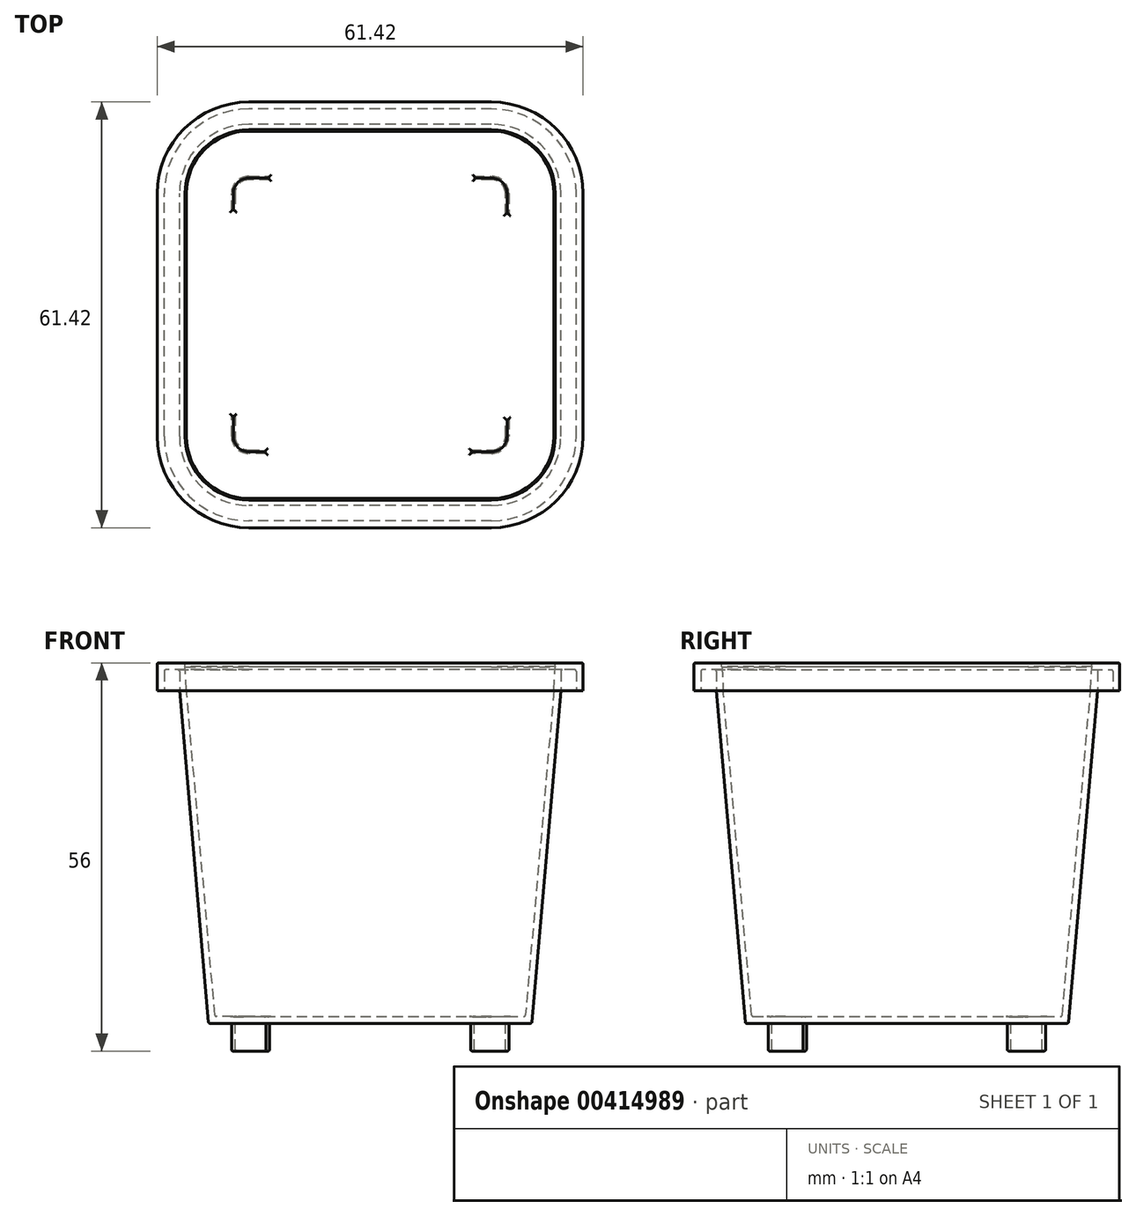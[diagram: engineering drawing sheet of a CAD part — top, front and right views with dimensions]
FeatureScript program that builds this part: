
annotation { "Feature Type Name" : "Feature", "Feature Type Description" : "" }
export const myFeature = defineFeature(function(context is Context, id is Id, definition is map)
    precondition{}
    {
        {
            var Q0;
            Q0=qCreatedBy(makeId("Top.planeOp"),FACE);
            var sketch = newSketch(context, id + "F0", { "sketchPlane" : qUnion([Q0])});
            skLineSegment(sketch, "E0.bottom", {"start": v(17.5, -27.5) * mm, "end": v(-17.5, -27.5) * mm});
            skLineSegment(sketch, "E0.top", {"start": v(17.5, 27.5) * mm, "end": v(-17.5, 27.5) * mm});
            skLineSegment(sketch, "E0.left", {"start": v(27.5, -17.5) * mm, "end": v(27.5, 17.5) * mm});
            skLineSegment(sketch, "E0.right", {"start": v(-27.5, -17.5) * mm, "end": v(-27.5, 17.5) * mm});
            skPoint(sketch, "E0.middle", {"position": v(0, 0) * mm});
            skPoint(sketch, "E1.visualSharp", {"position": v(-27.5, 27.5) * mm});
            skArc(sketch, "E1.filletArc", {"start": v(-17.5, 27.5) * mm, "mid": v(-24.57, 24.57) * mm, "end": v(-27.5, 17.5) * mm});
            skPoint(sketch, "E2.visualSharp", {"position": v(-27.5, -27.5) * mm});
            skArc(sketch, "E2.filletArc", {"start": v(-27.5, -17.5) * mm, "mid": v(-24.57, -24.57) * mm, "end": v(-17.5, -27.5) * mm});
            skPoint(sketch, "E3.visualSharp", {"position": v(27.5, -27.5) * mm});
            skArc(sketch, "E3.filletArc", {"start": v(17.5, -27.5) * mm, "mid": v(24.57, -24.57) * mm, "end": v(27.5, -17.5) * mm});
            skPoint(sketch, "E4.visualSharp", {"position": v(27.5, 27.5) * mm});
            skArc(sketch, "E4.filletArc", {"start": v(27.5, 17.5) * mm, "mid": v(24.57, 24.57) * mm, "end": v(17.5, 27.5) * mm});
            skSolve(sketch);
        }
        {
            var Q0;
            Q0 = qSketchRegion(id + "F0", true);
            extrude(context, id + "F1", {"entities" : qUnion([Q0]), "depth" : 4 * mm, "hasDraft" : true, "draftAngle" : 3 * degree, "hasSecondDirectionDraft" : true, "secondDirectionDraftAngle" : 3 * degree});
        }
        {
            var Q0;
            Q0=makeQuery(id+"F1.opExtrude","CAP_FACE",FACE,{"disambiguationData":[OSD([sQuery(id+"F0.wireOp",EDGE,"E0.bottom"),sQuery(id+"F0.wireOp",EDGE,"E0.top"),sQuery(id+"F0.wireOp",EDGE,"E0.left"),sQuery(id+"F0.wireOp",EDGE,"E0.right"),sQuery(id+"F0.wireOp",EDGE,"E1.filletArc"),sQuery(id+"F0.wireOp",EDGE,"E2.filletArc"),sQuery(id+"F0.wireOp",EDGE,"E3.filletArc"),sQuery(id+"F0.wireOp",EDGE,"E4.filletArc")])],"isStart":true});
            extrude(context, id + "F2", {"entities" : qUnion([Q0]), "operationType" : NewBodyOperationType.ADD, "depth" : 48 * mm, "hasDraft" : true, "draftAngle" : 5 * degree, "draftPullDirection" : true});
        }
        {
            var Q0;
            Q0=makeQuery(id+"F1.opExtrude","CAP_FACE",FACE,{"disambiguationData":[OSD([sQuery(id+"F0.wireOp",EDGE,"E0.bottom"),sQuery(id+"F0.wireOp",EDGE,"E0.top"),sQuery(id+"F0.wireOp",EDGE,"E0.left"),sQuery(id+"F0.wireOp",EDGE,"E0.right"),sQuery(id+"F0.wireOp",EDGE,"E1.filletArc"),sQuery(id+"F0.wireOp",EDGE,"E2.filletArc"),sQuery(id+"F0.wireOp",EDGE,"E3.filletArc"),sQuery(id+"F0.wireOp",EDGE,"E4.filletArc")])],"isStart":false});
            shell(context, id + "F3", {"entities" : qUnion([Q0]), "thickness" : 1 * mm});
        }
        {
            var Q0;
            Q0=makeQuery(id+"F1.opExtrude","CAP_FACE",FACE,{"disambiguationData":[OSD([sQuery(id+"F0.wireOp",EDGE,"E0.bottom"),sQuery(id+"F0.wireOp",EDGE,"E0.top"),sQuery(id+"F0.wireOp",EDGE,"E0.left"),sQuery(id+"F0.wireOp",EDGE,"E0.right"),sQuery(id+"F0.wireOp",EDGE,"E1.filletArc"),sQuery(id+"F0.wireOp",EDGE,"E2.filletArc"),sQuery(id+"F0.wireOp",EDGE,"E3.filletArc"),sQuery(id+"F0.wireOp",EDGE,"E4.filletArc")])],"isStart":false});
            var sketch = newSketch(context, id + "F4", { "sketchPlane" : qUnion([Q0])});
            skLineSegment(sketch, "E5.0", {"start": v(17.5, 30.7) * mm, "end": v(-17.5, 30.7) * mm});
            skArc(sketch, "E5.1", {"start": v(30.7, 17.5) * mm, "mid": v(26.84, 26.84) * mm, "end": v(17.5, 30.7) * mm});
            skArc(sketch, "E5.2", {"start": v(-17.5, 30.7) * mm, "mid": v(-26.84, 26.84) * mm, "end": v(-30.7, 17.5) * mm});
            skLineSegment(sketch, "E5.3", {"start": v(30.7, -17.5) * mm, "end": v(30.7, 17.5) * mm});
            skLineSegment(sketch, "E5.4", {"start": v(-30.7, -17.5) * mm, "end": v(-30.7, 17.5) * mm});
            skArc(sketch, "E5.5", {"start": v(-30.7, -17.5) * mm, "mid": v(-26.84, -26.84) * mm, "end": v(-17.5, -30.7) * mm});
            skLineSegment(sketch, "E5.6", {"start": v(17.5, -30.7) * mm, "end": v(-17.5, -30.7) * mm});
            skArc(sketch, "E5.7", {"start": v(17.5, -30.7) * mm, "mid": v(26.84, -26.84) * mm, "end": v(30.7, -17.5) * mm});
            skArc(sketch, "E6.0", {"start": v(-17.5, 26.7) * mm, "mid": v(-24.01, 24.01) * mm, "end": v(-26.7, 17.5) * mm});
            skLineSegment(sketch, "E7.0", {"start": v(-26.7, -17.5) * mm, "end": v(-26.7, 17.5) * mm});
            skArc(sketch, "E8.0", {"start": v(-26.7, -17.5) * mm, "mid": v(-24.01, -24.01) * mm, "end": v(-17.5, -26.7) * mm});
            skLineSegment(sketch, "E9.0", {"start": v(17.5, -26.7) * mm, "end": v(-17.5, -26.7) * mm});
            skArc(sketch, "E10.0", {"start": v(17.5, -26.7) * mm, "mid": v(24.01, -24.01) * mm, "end": v(26.7, -17.5) * mm});
            skLineSegment(sketch, "E11.0", {"start": v(26.7, -17.5) * mm, "end": v(26.7, 17.5) * mm});
            skArc(sketch, "E12.0", {"start": v(26.7, 17.5) * mm, "mid": v(24.01, 24.01) * mm, "end": v(17.5, 26.7) * mm});
            skLineSegment(sketch, "E13.0", {"start": v(17.5, 26.7) * mm, "end": v(-17.5, 26.7) * mm});
            skSolve(sketch);
        }
        {
            var Q0;
            Q0 = qSketchRegion(id + "F4", true);
            extrude(context, id + "F5", {"entities" : qUnion([Q0]), "operationType" : NewBodyOperationType.ADD, "oppositeDirection" : true, "depth" : 4 * mm});
        }
        {
            var Q0;
            Q0=makeQuery(id+"F5.opExtrude","CAP_FACE",FACE,{"disambiguationData":[OSD([sQuery(id+"F4.wireOp",EDGE,"E5.0"),sQuery(id+"F4.wireOp",EDGE,"E5.1"),sQuery(id+"F4.wireOp",EDGE,"E5.2"),sQuery(id+"F4.wireOp",EDGE,"E5.3"),sQuery(id+"F4.wireOp",EDGE,"E5.4"),sQuery(id+"F4.wireOp",EDGE,"E5.5"),sQuery(id+"F4.wireOp",EDGE,"E5.6"),sQuery(id+"F4.wireOp",EDGE,"E5.7"),sQuery(id+"F4.wireOp",EDGE,"E6.0"),sQuery(id+"F4.wireOp",EDGE,"E7.0"),sQuery(id+"F4.wireOp",EDGE,"E8.0"),sQuery(id+"F4.wireOp",EDGE,"E9.0"),sQuery(id+"F4.wireOp",EDGE,"E10.0"),sQuery(id+"F4.wireOp",EDGE,"E11.0"),sQuery(id+"F4.wireOp",EDGE,"E12.0"),sQuery(id+"F4.wireOp",EDGE,"E13.0")])],"isStart":false});
            var sketch = newSketch(context, id + "F6", { "sketchPlane" : qUnion([Q0])});
            skArc(sketch, "E14.0", {"start": v(-27.5, 17.5) * mm, "mid": v(-24.57, 24.57) * mm, "end": v(-17.5, 27.5) * mm});
            skLineSegment(sketch, "E14.1", {"start": v(17.5, 27.5) * mm, "end": v(-17.5, 27.5) * mm});
            skArc(sketch, "E14.2", {"start": v(-17.5, -27.5) * mm, "mid": v(-24.57, -24.57) * mm, "end": v(-27.5, -17.5) * mm});
            skLineSegment(sketch, "E14.3", {"start": v(-27.5, 17.5) * mm, "end": v(-27.5, -17.5) * mm});
            skLineSegment(sketch, "E14.4", {"start": v(27.5, 17.5) * mm, "end": v(27.5, -17.5) * mm});
            skArc(sketch, "E14.5", {"start": v(17.5, 27.5) * mm, "mid": v(24.57, 24.57) * mm, "end": v(27.5, 17.5) * mm});
            skArc(sketch, "E14.6", {"start": v(27.5, -17.5) * mm, "mid": v(24.57, -24.57) * mm, "end": v(17.5, -27.5) * mm});
            skLineSegment(sketch, "E14.7", {"start": v(17.5, -27.5) * mm, "end": v(-17.5, -27.5) * mm});
            skArc(sketch, "E15.0", {"start": v(-29.7, 17.5) * mm, "mid": v(-26.13, 26.13) * mm, "end": v(-17.5, 29.7) * mm});
            skLineSegment(sketch, "E15.1", {"start": v(-29.7, 17.5) * mm, "end": v(-29.7, -17.5) * mm});
            skArc(sketch, "E16.0", {"start": v(-17.5, -29.7) * mm, "mid": v(-26.13, -26.13) * mm, "end": v(-29.7, -17.5) * mm});
            skLineSegment(sketch, "E16.1", {"start": v(17.5, -29.7) * mm, "end": v(-17.5, -29.7) * mm});
            skLineSegment(sketch, "E16.2", {"start": v(17.5, 29.7) * mm, "end": v(-17.5, 29.7) * mm});
            skArc(sketch, "E16.3", {"start": v(17.5, 29.7) * mm, "mid": v(26.13, 26.13) * mm, "end": v(29.7, 17.5) * mm});
            skLineSegment(sketch, "E16.4", {"start": v(29.7, 17.5) * mm, "end": v(29.7, -17.5) * mm});
            skArc(sketch, "E16.5", {"start": v(29.7, -17.5) * mm, "mid": v(26.13, -26.13) * mm, "end": v(17.5, -29.7) * mm});
            skSolve(sketch);
        }
        {
            var Q0;
            Q0 = qSketchRegion(id + "F6", true);
            extrude(context, id + "F7", {"entities" : qUnion([Q0]), "operationType" : NewBodyOperationType.REMOVE, "oppositeDirection" : true, "depth" : 3 * mm});
        }
        {
            var Q0;
            Q0=makeQuery(id+"F2.opExtrude","CAP_FACE",FACE,{"disambiguationData":[OSD([sQuery(id+"F0.wireOp",EDGE,"E0.bottom"),sQuery(id+"F0.wireOp",EDGE,"E0.top"),sQuery(id+"F0.wireOp",EDGE,"E0.left"),sQuery(id+"F0.wireOp",EDGE,"E0.right"),sQuery(id+"F0.wireOp",EDGE,"E1.filletArc"),sQuery(id+"F0.wireOp",EDGE,"E2.filletArc"),sQuery(id+"F0.wireOp",EDGE,"E3.filletArc"),sQuery(id+"F0.wireOp",EDGE,"E4.filletArc")])],"isStart":false});
            var sketch = newSketch(context, id + "F8", { "sketchPlane" : qUnion([Q0])});
            skLineSegment(sketch, "E17", {"start": v(-15, 20) * mm, "end": v(-17.5, 20) * mm});
            skLineSegment(sketch, "E18", {"start": v(-20, 17.5) * mm, "end": v(-20, 14.5) * mm});
            skLineSegment(sketch, "E19", {"start": v(-20, 14.5) * mm, "end": v(-19.5, 14.5) * mm});
            skLineSegment(sketch, "E20", {"start": v(-19.5, 14.5) * mm, "end": v(-19.5, 17.5) * mm});
            skLineSegment(sketch, "E21", {"start": v(-17.5, 19.5) * mm, "end": v(-15, 19.5) * mm});
            skLineSegment(sketch, "E22", {"start": v(-15, 19.5) * mm, "end": v(-15, 20) * mm});
            skPoint(sketch, "E23.visualSharp", {"position": v(-19.5, 19.5) * mm});
            skArc(sketch, "E23.filletArc", {"start": v(-17.5, 19.5) * mm, "mid": v(-18.91, 18.91) * mm, "end": v(-19.5, 17.5) * mm});
            skPoint(sketch, "E24.visualSharp", {"position": v(-20, 20) * mm});
            skArc(sketch, "E24.filletArc", {"start": v(-17.5, 20) * mm, "mid": v(-19.27, 19.27) * mm, "end": v(-20, 17.5) * mm});
            skLineSegment(sketch, "E25.1.0", {"start": v(19.5, 15) * mm, "end": v(20, 15) * mm});
            skLineSegment(sketch, "E25.1.1", {"start": v(14.5, 19.5) * mm, "end": v(17.5, 19.5) * mm});
            skLineSegment(sketch, "E25.1.2", {"start": v(17.5, 20) * mm, "end": v(14.5, 20) * mm});
            skLineSegment(sketch, "E25.1.3", {"start": v(19.5, 17.5) * mm, "end": v(19.5, 15) * mm});
            skLineSegment(sketch, "E25.1.4", {"start": v(20, 15) * mm, "end": v(20, 17.5) * mm});
            skArc(sketch, "E25.1.5", {"start": v(20, 17.5) * mm, "mid": v(19.27, 19.27) * mm, "end": v(17.5, 20) * mm});
            skArc(sketch, "E25.1.6", {"start": v(19.5, 17.5) * mm, "mid": v(18.91, 18.91) * mm, "end": v(17.5, 19.5) * mm});
            skLineSegment(sketch, "E25.1.7", {"start": v(14.5, 20) * mm, "end": v(14.5, 19.5) * mm});
            skLineSegment(sketch, "E25.2.0", {"start": v(15, -19.5) * mm, "end": v(15, -20) * mm});
            skLineSegment(sketch, "E25.2.1", {"start": v(19.5, -14.5) * mm, "end": v(19.5, -17.5) * mm});
            skLineSegment(sketch, "E25.2.2", {"start": v(20, -17.5) * mm, "end": v(20, -14.5) * mm});
            skLineSegment(sketch, "E25.2.3", {"start": v(17.5, -19.5) * mm, "end": v(15, -19.5) * mm});
            skLineSegment(sketch, "E25.2.4", {"start": v(15, -20) * mm, "end": v(17.5, -20) * mm});
            skArc(sketch, "E25.2.5", {"start": v(17.5, -20) * mm, "mid": v(19.27, -19.27) * mm, "end": v(20, -17.5) * mm});
            skArc(sketch, "E25.2.6", {"start": v(17.5, -19.5) * mm, "mid": v(18.91, -18.91) * mm, "end": v(19.5, -17.5) * mm});
            skLineSegment(sketch, "E25.2.7", {"start": v(20, -14.5) * mm, "end": v(19.5, -14.5) * mm});
            skLineSegment(sketch, "E25.3.0", {"start": v(-19.5, -15) * mm, "end": v(-20, -15) * mm});
            skLineSegment(sketch, "E25.3.1", {"start": v(-14.5, -19.5) * mm, "end": v(-17.5, -19.5) * mm});
            skLineSegment(sketch, "E25.3.2", {"start": v(-17.5, -20) * mm, "end": v(-14.5, -20) * mm});
            skLineSegment(sketch, "E25.3.3", {"start": v(-19.5, -17.5) * mm, "end": v(-19.5, -15) * mm});
            skLineSegment(sketch, "E25.3.4", {"start": v(-20, -15) * mm, "end": v(-20, -17.5) * mm});
            skArc(sketch, "E25.3.5", {"start": v(-20, -17.5) * mm, "mid": v(-19.27, -19.27) * mm, "end": v(-17.5, -20) * mm});
            skArc(sketch, "E25.3.6", {"start": v(-19.5, -17.5) * mm, "mid": v(-18.91, -18.91) * mm, "end": v(-17.5, -19.5) * mm});
            skLineSegment(sketch, "E25.3.7", {"start": v(-14.5, -20) * mm, "end": v(-14.5, -19.5) * mm});
            skPoint(sketch, "E25.center", {"position": v(0, 0) * mm});
            skLineSegment(sketch, "E25.anchor1", {"start": v(0, 0) * mm, "end": v(-15, 19.5) * mm, "construction": true});
            skLineSegment(sketch, "E25.anchor2", {"start": v(0, 0) * mm, "end": v(-19.5, -15) * mm, "construction": true});
            skSolve(sketch);
        }
        {
            var Q0;
            Q0 = qSketchRegion(id + "F8", true);
            extrude(context, id + "F9", {"entities" : qUnion([Q0]), "operationType" : NewBodyOperationType.ADD, "depth" : 4 * mm});
        }
        {
            var Q0;
            Q0=makeQuery(id+"F3.opShell","OFFSET_FACE",FACE,{"disambiguationData":[OSD([sQuery(id+"F0.wireOp",EDGE,"E0.bottom"),sQuery(id+"F0.wireOp",EDGE,"E0.top"),sQuery(id+"F0.wireOp",EDGE,"E0.left"),sQuery(id+"F0.wireOp",EDGE,"E0.right"),sQuery(id+"F0.wireOp",EDGE,"E1.filletArc"),sQuery(id+"F0.wireOp",EDGE,"E2.filletArc"),sQuery(id+"F0.wireOp",EDGE,"E3.filletArc"),sQuery(id+"F0.wireOp",EDGE,"E4.filletArc")])]});
            var Q1;
            Q1=makeQuery(id+"F2.opExtrude","CAP_FACE",FACE,{"disambiguationData":[OSD([sQuery(id+"F0.wireOp",EDGE,"E0.bottom"),sQuery(id+"F0.wireOp",EDGE,"E0.top"),sQuery(id+"F0.wireOp",EDGE,"E0.left"),sQuery(id+"F0.wireOp",EDGE,"E0.right"),sQuery(id+"F0.wireOp",EDGE,"E1.filletArc"),sQuery(id+"F0.wireOp",EDGE,"E2.filletArc"),sQuery(id+"F0.wireOp",EDGE,"E3.filletArc"),sQuery(id+"F0.wireOp",EDGE,"E4.filletArc")])],"isStart":false});
            var Q2;
            Q2=makeQuery(id+"F7.boolean.opBoolean","COPY",FACE,{"derivedFrom":makeQuery(id+"F7.opExtrude","CAP_FACE",FACE,{"disambiguationData":[OSD([sQuery(id+"F6.wireOp",EDGE,"E14.0"),sQuery(id+"F6.wireOp",EDGE,"E14.1"),sQuery(id+"F6.wireOp",EDGE,"E14.2"),sQuery(id+"F6.wireOp",EDGE,"E14.3"),sQuery(id+"F6.wireOp",EDGE,"E14.4"),sQuery(id+"F6.wireOp",EDGE,"E14.5"),sQuery(id+"F6.wireOp",EDGE,"E14.6"),sQuery(id+"F6.wireOp",EDGE,"E14.7"),sQuery(id+"F6.wireOp",EDGE,"E15.0"),sQuery(id+"F6.wireOp",EDGE,"E15.1"),sQuery(id+"F6.wireOp",EDGE,"E16.0"),sQuery(id+"F6.wireOp",EDGE,"E16.1"),sQuery(id+"F6.wireOp",EDGE,"E16.2"),sQuery(id+"F6.wireOp",EDGE,"E16.3"),sQuery(id+"F6.wireOp",EDGE,"E16.4"),sQuery(id+"F6.wireOp",EDGE,"E16.5")])],"isStart":false})});
            var Q3;
            Q3=makeQuery(id+"F5.boolean.opBoolean","MERGE",FACE,{"derivedFrom":[makeQuery(id+"F1.opExtrude","CAP_FACE",FACE,{"disambiguationData":[OSD([sQuery(id+"F0.wireOp",EDGE,"E0.bottom"),sQuery(id+"F0.wireOp",EDGE,"E0.top"),sQuery(id+"F0.wireOp",EDGE,"E0.left"),sQuery(id+"F0.wireOp",EDGE,"E0.right"),sQuery(id+"F0.wireOp",EDGE,"E1.filletArc"),sQuery(id+"F0.wireOp",EDGE,"E2.filletArc"),sQuery(id+"F0.wireOp",EDGE,"E3.filletArc"),sQuery(id+"F0.wireOp",EDGE,"E4.filletArc")])],"isStart":false}),makeQuery(id+"F5.opExtrude","CAP_FACE",FACE,{"disambiguationData":[OSD([sQuery(id+"F4.wireOp",EDGE,"E5.0"),sQuery(id+"F4.wireOp",EDGE,"E5.1"),sQuery(id+"F4.wireOp",EDGE,"E5.2"),sQuery(id+"F4.wireOp",EDGE,"E5.3"),sQuery(id+"F4.wireOp",EDGE,"E5.4"),sQuery(id+"F4.wireOp",EDGE,"E5.5"),sQuery(id+"F4.wireOp",EDGE,"E5.6"),sQuery(id+"F4.wireOp",EDGE,"E5.7"),sQuery(id+"F4.wireOp",EDGE,"E6.0"),sQuery(id+"F4.wireOp",EDGE,"E7.0"),sQuery(id+"F4.wireOp",EDGE,"E8.0"),sQuery(id+"F4.wireOp",EDGE,"E9.0"),sQuery(id+"F4.wireOp",EDGE,"E10.0"),sQuery(id+"F4.wireOp",EDGE,"E11.0"),sQuery(id+"F4.wireOp",EDGE,"E12.0"),sQuery(id+"F4.wireOp",EDGE,"E13.0")])],"isStart":true})]});
            var Q4;
            Q4=makeQuery(id+"F9.opExtrude","CAP_FACE",FACE,{"disambiguationData":[OSD([sQuery(id+"F8.wireOp",EDGE,"E25.3.0"),sQuery(id+"F8.wireOp",EDGE,"E25.3.1"),sQuery(id+"F8.wireOp",EDGE,"E25.3.2"),sQuery(id+"F8.wireOp",EDGE,"E25.3.3"),sQuery(id+"F8.wireOp",EDGE,"E25.3.4"),sQuery(id+"F8.wireOp",EDGE,"E25.3.5"),sQuery(id+"F8.wireOp",EDGE,"E25.3.6"),sQuery(id+"F8.wireOp",EDGE,"E25.3.7")])],"isStart":false});
            var Q5;
            Q5=makeQuery(id+"F9.opExtrude","CAP_FACE",FACE,{"disambiguationData":[OSD([sQuery(id+"F8.wireOp",EDGE,"E17"),sQuery(id+"F8.wireOp",EDGE,"E18"),sQuery(id+"F8.wireOp",EDGE,"E19"),sQuery(id+"F8.wireOp",EDGE,"E20"),sQuery(id+"F8.wireOp",EDGE,"E21"),sQuery(id+"F8.wireOp",EDGE,"E22"),sQuery(id+"F8.wireOp",EDGE,"E23.filletArc"),sQuery(id+"F8.wireOp",EDGE,"E24.filletArc")])],"isStart":false});
            var Q6;
            Q6=makeQuery(id+"F9.opExtrude","CAP_FACE",FACE,{"disambiguationData":[OSD([sQuery(id+"F8.wireOp",EDGE,"E25.1.0"),sQuery(id+"F8.wireOp",EDGE,"E25.1.1"),sQuery(id+"F8.wireOp",EDGE,"E25.1.2"),sQuery(id+"F8.wireOp",EDGE,"E25.1.3"),sQuery(id+"F8.wireOp",EDGE,"E25.1.4"),sQuery(id+"F8.wireOp",EDGE,"E25.1.5"),sQuery(id+"F8.wireOp",EDGE,"E25.1.6"),sQuery(id+"F8.wireOp",EDGE,"E25.1.7")])],"isStart":false});
            var Q7;
            Q7=makeQuery(id+"F9.opExtrude","CAP_FACE",FACE,{"disambiguationData":[OSD([sQuery(id+"F8.wireOp",EDGE,"E25.2.0"),sQuery(id+"F8.wireOp",EDGE,"E25.2.1"),sQuery(id+"F8.wireOp",EDGE,"E25.2.2"),sQuery(id+"F8.wireOp",EDGE,"E25.2.3"),sQuery(id+"F8.wireOp",EDGE,"E25.2.4"),sQuery(id+"F8.wireOp",EDGE,"E25.2.5"),sQuery(id+"F8.wireOp",EDGE,"E25.2.6"),sQuery(id+"F8.wireOp",EDGE,"E25.2.7")])],"isStart":false});
            fillet(context, id + "F10", {"entities" : qUnion([Q0, Q1, Q2, Q3, Q4, Q5, Q6, Q7]), "radius" : .2 * mm, "tangentPropagation" : true, "allowEdgeOverflow" : false});
        }
    });
